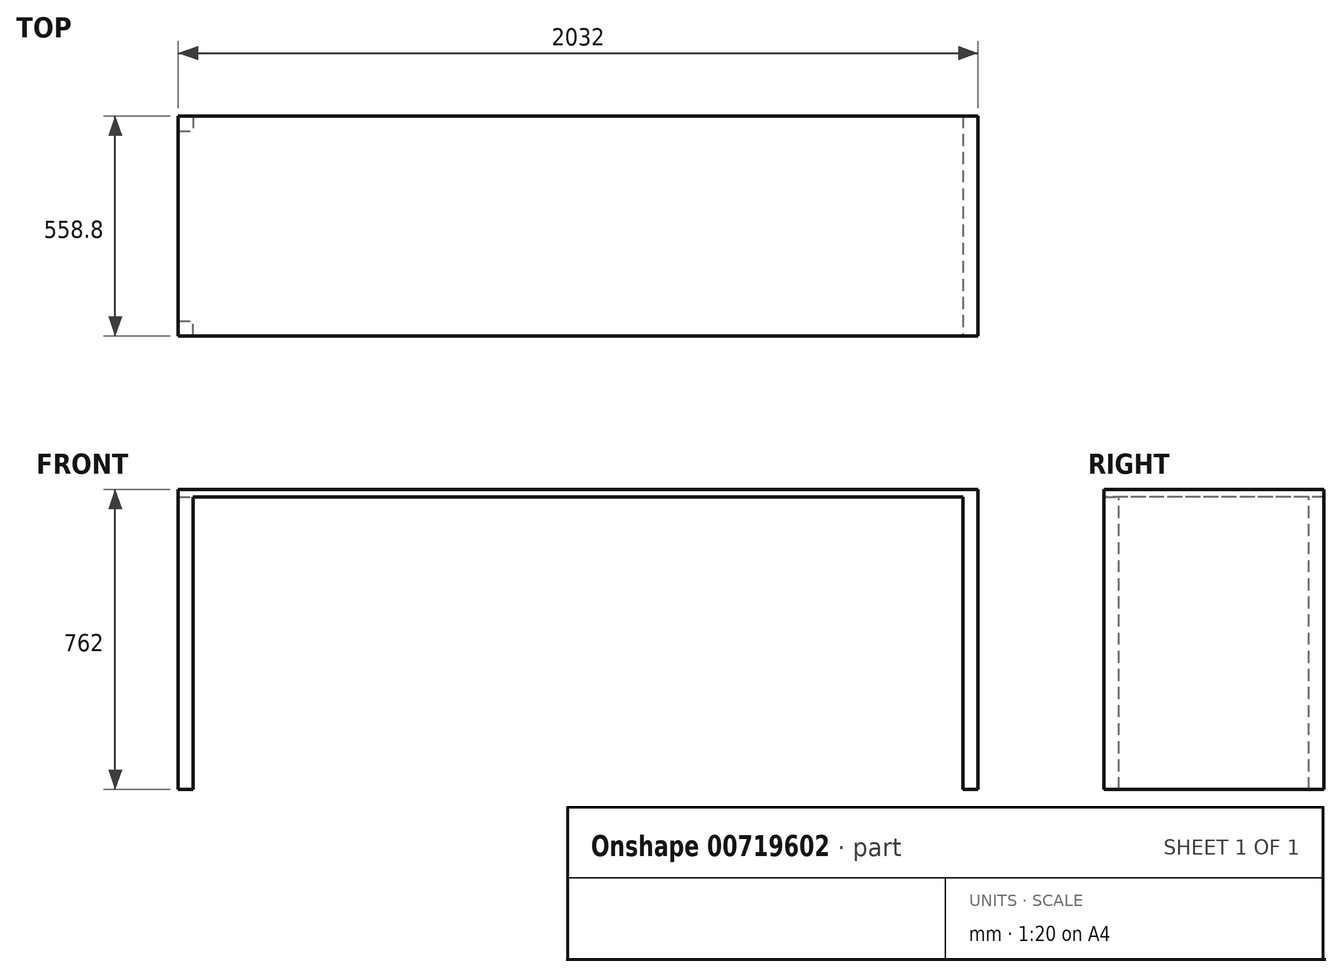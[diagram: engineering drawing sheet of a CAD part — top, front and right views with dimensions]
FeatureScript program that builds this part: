
annotation { "Feature Type Name" : "Feature", "Feature Type Description" : "" }
export const myFeature = defineFeature(function(context is Context, id is Id, definition is map)
    precondition{}
    {
        {
            var Q0;
            Q0=qCreatedBy(makeId("Top.planeOp"),FACE);
            cPlane(context, id + "F0", {"entities" : qUnion([Q0]), "cplaneType" : CPlaneType.OFFSET, "offset" : 762 * mm, "width" : 152.4 * mm, "height" : 152.4 * mm});
        }
        {
            var Q0;
            Q0=qCreatedBy(id+"F0.planeOp",FACE);
            var sketch = newSketch(context, id + "F1", { "sketchPlane" : qUnion([Q0])});
            skLineSegment(sketch, "E0.bottom", {"start": v(0, 558.8) * mm, "end": v(2032, 558.8) * mm});
            skLineSegment(sketch, "E0.top", {"start": v(0, 0) * mm, "end": v(2032, 0) * mm});
            skLineSegment(sketch, "E0.left", {"start": v(0, 558.8) * mm, "end": v(0, 0) * mm});
            skLineSegment(sketch, "E0.right", {"start": v(2032, 558.8) * mm, "end": v(2032, 0) * mm});
            skSolve(sketch);
        }
        {
            var Q0;
            Q0=makeQuery(id+"F1.imprint","IMPRINT",FACE,{"disambiguationData":[TD([[makeQuery(id+"F1.imprint","IMPRINT",EDGE,{"derivedFrom":sQuery(id+"F1.wireOp",EDGE,"E0.bottom")}),-1.0]])]});
            extrude(context, id + "F2", {"entities" : qUnion([Q0]), "oppositeDirection" : true, "depth" : 19.05 * mm, "offsetDistance" : 25.4 * mm});
        }
        {
            var Q0;
            Q0=makeQuery(id+"F2.opExtrude","CAP_FACE",FACE,{"disambiguationData":[OSD([sQuery(id+"F1.wireOp",EDGE,"E0.bottom"),sQuery(id+"F1.wireOp",EDGE,"E0.top"),sQuery(id+"F1.wireOp",EDGE,"E0.left"),sQuery(id+"F1.wireOp",EDGE,"E0.right")])],"isStart":false});
            var sketch = newSketch(context, id + "F3", { "sketchPlane" : qUnion([Q0])});
            skLineSegment(sketch, "E1.bottom", {"start": v(0, 0) * mm, "end": v(38.1, 0) * mm});
            skLineSegment(sketch, "E1.top", {"start": v(0, -38.1) * mm, "end": v(38.1, -38.1) * mm});
            skLineSegment(sketch, "E1.left", {"start": v(0, 0) * mm, "end": v(0, -38.1) * mm});
            skLineSegment(sketch, "E1.right", {"start": v(38.1, 0) * mm, "end": v(38.1, -38.1) * mm});
            skLineSegment(sketch, "E2.bottom", {"start": v(0, -558.8) * mm, "end": v(38.1, -558.8) * mm});
            skLineSegment(sketch, "E2.top", {"start": v(0, -520.7) * mm, "end": v(38.1, -520.7) * mm});
            skLineSegment(sketch, "E2.left", {"start": v(0, -558.8) * mm, "end": v(0, -520.7) * mm});
            skLineSegment(sketch, "E2.right", {"start": v(38.1, -558.8) * mm, "end": v(38.1, -520.7) * mm});
            skLineSegment(sketch, "E3.bottom", {"start": v(2032, -558.8) * mm, "end": v(1993.9, -558.8) * mm});
            skLineSegment(sketch, "E3.top", {"start": v(2032, 0) * mm, "end": v(1993.9, 0) * mm});
            skLineSegment(sketch, "E3.left", {"start": v(2032, -558.8) * mm, "end": v(2032, 0) * mm});
            skLineSegment(sketch, "E3.right", {"start": v(1993.9, -558.8) * mm, "end": v(1993.9, 0) * mm});
            skSolve(sketch);
        }
        {
            var Q0;
            Q0=makeQuery(id+"F3.imprint","IMPRINT",FACE,{"disambiguationData":[TD([[makeQuery(id+"F3.imprint","IMPRINT",EDGE,{"derivedFrom":sQuery(id+"F3.wireOp",EDGE,"E1.bottom")}),-1.0]])]});
            var Q1;
            Q1=makeQuery(id+"F3.imprint","IMPRINT",FACE,{"disambiguationData":[TD([[makeQuery(id+"F3.imprint","IMPRINT",EDGE,{"derivedFrom":sQuery(id+"F3.wireOp",EDGE,"E2.bottom")}),1.0]])]});
            var Q2;
            Q2=makeQuery(id+"F3.imprint","IMPRINT",FACE,{"disambiguationData":[TD([[makeQuery(id+"F3.imprint","IMPRINT",EDGE,{"derivedFrom":sQuery(id+"F3.wireOp",EDGE,"E3.bottom")}),1.0]])]});
            var Q3;
            Q3=qCreatedBy(makeId("Top.planeOp"),FACE);
            extrude(context, id + "F4", {"entities" : qUnion([Q0, Q1, Q2]), "operationType" : NewBodyOperationType.ADD, "endBound" : BoundingType.UP_TO_SURFACE, "depth" : 25.4 * mm, "endBoundEntityFace" : qUnion([Q3]), "offsetDistance" : 25.4 * mm});
        }
    });
